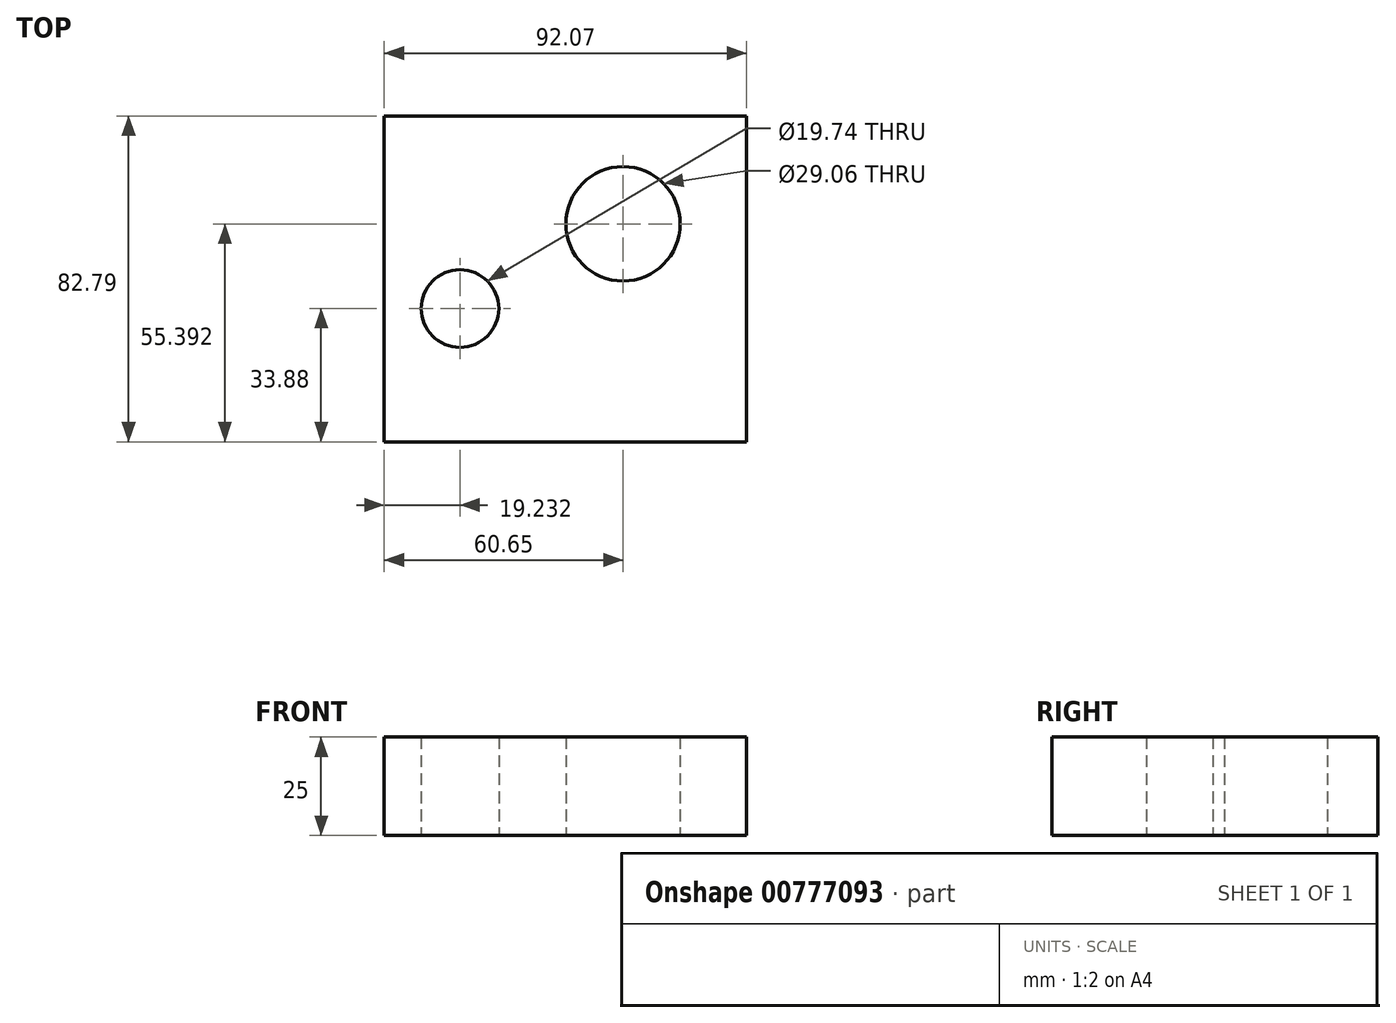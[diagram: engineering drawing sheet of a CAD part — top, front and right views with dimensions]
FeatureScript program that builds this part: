
annotation { "Feature Type Name" : "Feature", "Feature Type Description" : "" }
export const myFeature = defineFeature(function(context is Context, id is Id, definition is map)
    precondition{}
    {
        {
            var Q0;
            Q0=qCreatedBy(makeId("Top.planeOp"),FACE);
            var sketch = newSketch(context, id + "F0", { "sketchPlane" : qUnion([Q0])});
            skLineSegment(sketch, "E0.bottom", {"start": v(-45.05, -33.88) * mm, "end": v(47.02, -33.88) * mm});
            skLineSegment(sketch, "E0.top", {"start": v(-45.05, 48.91) * mm, "end": v(47.02, 48.91) * mm});
            skLineSegment(sketch, "E0.left", {"start": v(-45.05, -33.88) * mm, "end": v(-45.05, 48.91) * mm});
            skLineSegment(sketch, "E0.right", {"start": v(47.02, -33.88) * mm, "end": v(47.02, 48.91) * mm});
            skCircle(sketch, "E1", {"center": v(-25.82, 0) * mm, "radius": 9.87 * mm});
            skCircle(sketch, "E2", {"center": v(15.6, 21.51) * mm, "radius": 14.53 * mm});
            skSolve(sketch);
        }
        {
            var Q0;
            Q0 = qSketchRegion(id + "F0", true);
            extrude(context, id + "F1", {"entities" : qUnion([Q0]), "depth" : 25 * mm, "offsetDistance" : 25 * mm});
        }
    });
